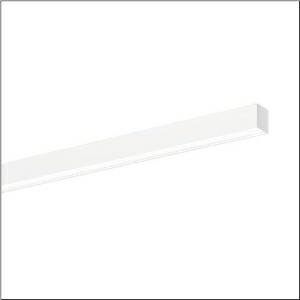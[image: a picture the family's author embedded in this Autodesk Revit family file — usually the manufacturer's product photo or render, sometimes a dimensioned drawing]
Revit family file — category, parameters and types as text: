
# Revit family: silica_r__21_51mx20dc45wb_dec1
name_source: partatom
category: Lighting Fixtures
units: mm (PartAtom-declared; Revit-internal decimal feet)

## family parameters
Cut with Voids When Loaded = No
Host = Face
Light Source = No
Part Type = Normal
Room Calculation Point = No
Round Connector Dimension = Use Diameter
Shared = No

## types (1)
- --- (1 x LED, 6000 lm, 40.1 W, 4000K)
    Apparent Load = 40 VA
    CIE Flux Codes = 48 79 96 100 100
    Color Rendering = 80
    Color Temperature = 4000K
    Default Elevation = 1800 mm
    Description = Silica® 21, office luminaire, primary optical cover: cover, of PMMA, opal, light emission: direct distribution, primary light characteristic: symmetric, installation type: surface-mounted, LED, rated luminous flux: 6.000lm, luminous efficacy: 150lm/W, light colour: 840, colour temperature: 4000K, control gear: DALI 2, with terminal, 3+2-pole, max. 2.5mm², mains connection: 220..240V, AC, 50/60Hz, rated input power: 40.1W, luminaire housing, of aluminium, traffic white (RAL 9016), length: 3.004mm, width: 53mm, height: 53mm, protection rating (complete): IP20, insulation class (complete): insulation class I (protective earthing), certification: CE, permissible operating ambient temperature: 0..+35°C, standard: EN 50419, packaging unit: 1 piece
    Height = 53 mm
    Lamp = 1 x LED
    Lamp Light Flux = 6000 lm
    Lamp Power = 40.1 W
    Lamp count = 1
    Length = 3004 mm
    Luminous efficacy = 150 lm/W
    Manufacturer = Siteco
    ModVariant = No
    Model = 51MX20DC45WB
    Mounting Place = Ceiling
    Mounting Type = Surface mounted
    Number of Poles = 1
    OnlyDefault = Yes
    Power Factor = 1
    Product Name = Silica® 21
    Product group = office luminaire | ceiling mounted
    ProductGroupID = 301
    Protection Class = Protection class I
    Protection Degree = IP 20
    RLX_Detail_Level = 1
    RLX_Emergency_Light_Flux = 0 lm
    RLX_Emergency_Type = 0
    RLX_Emergency_Type_DB = No
    RlxData = <blob elided: 23881 chars, md5=e15bd7f6>
    Socket = socket
    Standby Power = 0 W
    System Light Flux = 6000 lm
    System Power = 40 W
    Type Comments = factory setting: luminous flux: 100 % | dim-lin: 254 | 218 mA
    Type Image = l_1335877.jpg
    URL = http://relux.com
    VarID = @adj_115282
    Voltage = 0 V
    Weight = 0.00 kg
    Width = 53 mm

## geometry (parser evidence)
native form markers: Blend x4, Sweep x13
no freeform markers — native parametric forms only
